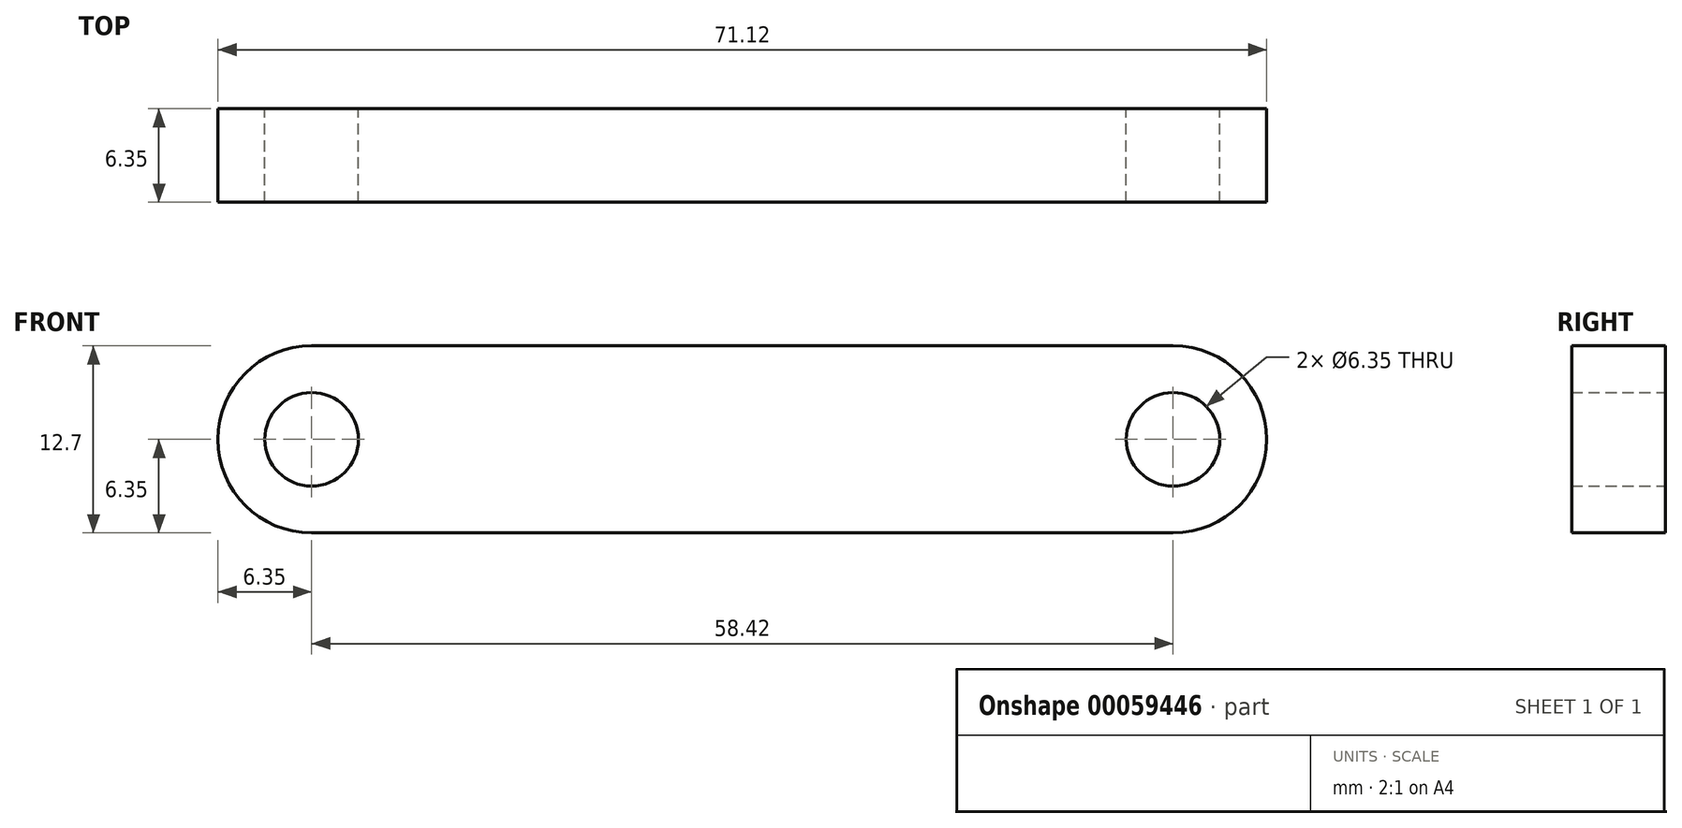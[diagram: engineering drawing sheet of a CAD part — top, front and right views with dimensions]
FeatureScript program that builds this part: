
annotation { "Feature Type Name" : "Feature", "Feature Type Description" : "" }
export const myFeature = defineFeature(function(context is Context, id is Id, definition is map)
    precondition{}
    {
        {
            var Q0;
            Q0=qCreatedBy(makeId("Front.planeOp"),FACE);
            var sketch = newSketch(context, id + "F0", { "sketchPlane" : qUnion([Q0])});
            skLineSegment(sketch, "E0.rect.bottom", {"start": v(29.21, -6.35) * mm, "end": v(-29.21, -6.35) * mm});
            skLineSegment(sketch, "E0.rect.top", {"start": v(29.21, 6.35) * mm, "end": v(-29.21, 6.35) * mm});
            skPoint(sketch, "E0.rect.middle", {"position": v(0, 0) * mm});
            skArc(sketch, "E1", {"start": v(-29.21, 6.35) * mm, "mid": v(-35.56, 0) * mm, "end": v(-29.21, -6.35) * mm});
            skArc(sketch, "E2", {"start": v(29.21, -6.35) * mm, "mid": v(35.56, 0) * mm, "end": v(29.21, 6.35) * mm});
            skCircle(sketch, "E3", {"center": v(-29.21, 0) * mm, "radius": 3.18 * mm});
            skCircle(sketch, "E4", {"center": v(29.21, 0) * mm, "radius": 3.18 * mm});
            skSolve(sketch);
        }
        {
            var Q0;
            Q0=makeQuery(id+"F0.imprint","IMPRINT",FACE,{"disambiguationData":[TD([[makeQuery(id+"F0.imprint","IMPRINT",EDGE,{"derivedFrom":sQuery(id+"F0.wireOp",EDGE,"E0.rect.bottom")}),-1.0]])]});
            extrude(context, id + "F1", {"entities" : qUnion([Q0]), "depth" : 6.35 * mm});
        }
    });
